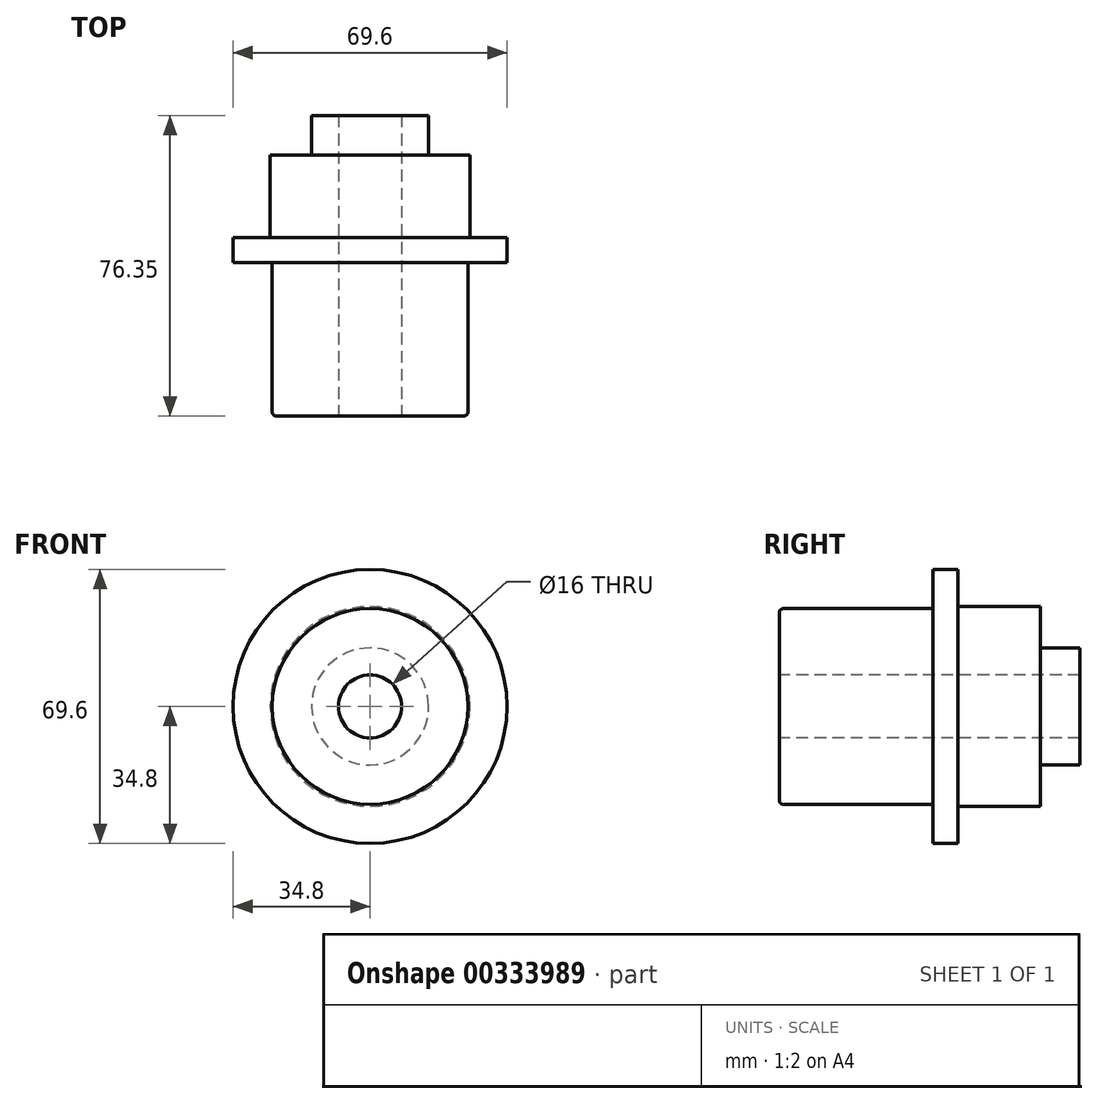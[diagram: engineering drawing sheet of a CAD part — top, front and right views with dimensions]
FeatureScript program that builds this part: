
annotation { "Feature Type Name" : "Feature", "Feature Type Description" : "" }
export const myFeature = defineFeature(function(context is Context, id is Id, definition is map)
    precondition{}
    {
        {
            var Q0;
            Q0=qCreatedBy(makeId("Front.planeOp"),FACE);
            var sketch = newSketch(context, id + "F0", { "sketchPlane" : qUnion([Q0])});
            skCircle(sketch, "E0", {"center": v(0, 0) * mm, "radius": 34.8 * mm});
            skSolve(sketch);
        }
        {
            var Q0;
            Q0 = qSketchRegion(id + "F0", true);
            extrude(context, id + "F1", {"entities" : qUnion([Q0]), "depth" : 6.35 * mm});
        }
        {
            var Q0;
            Q0=makeQuery(id+"F1.opExtrude","CAP_FACE",FACE,{"disambiguationData":[OSD([sQuery(id+"F0.wireOp",EDGE,"E0")])],"isStart":false});
            var sketch = newSketch(context, id + "F2", { "sketchPlane" : qUnion([Q0])});
            skCircle(sketch, "E1", {"center": v(0, 0) * mm, "radius": 24.85 * mm});
            skSolve(sketch);
        }
        {
            var Q0;
            Q0 = qSketchRegion(id + "F2", true);
            extrude(context, id + "F3", {"entities" : qUnion([Q0]), "operationType" : NewBodyOperationType.ADD, "depth" : 39 * mm});
        }
        {
            var Q0;
            Q0=makeQuery(id+"F3.opExtrude","CAP_EDGE",EDGE,{"disambiguationData":[OSD([sQuery(id+"F2.wireOp",EDGE,"E1")])],"isStart":false});
            fillet(context, id + "F4", {"entities" : qUnion([Q0]), "radius" : 1 * mm, "tangentPropagation" : true, "allowEdgeOverflow" : false});
        }
        {
            var Q0;
            Q0=makeQuery(id+"F1.opExtrude","CAP_FACE",FACE,{"disambiguationData":[OSD([sQuery(id+"F0.wireOp",EDGE,"E0")])],"isStart":true});
            var sketch = newSketch(context, id + "F5", { "sketchPlane" : qUnion([Q0])});
            skCircle(sketch, "E2", {"center": v(0, 0) * mm, "radius": 25.36 * mm});
            skSolve(sketch);
        }
        {
            var Q0;
            Q0 = qSketchRegion(id + "F5", true);
            extrude(context, id + "F6", {"entities" : qUnion([Q0]), "operationType" : NewBodyOperationType.ADD, "depth" : 21 * mm});
        }
        {
            var Q0;
            Q0=makeQuery(id+"F6.opExtrude","CAP_FACE",FACE,{"disambiguationData":[OSD([sQuery(id+"F5.wireOp",EDGE,"E2")])],"isStart":false});
            var sketch = newSketch(context, id + "F7", { "sketchPlane" : qUnion([Q0])});
            skCircle(sketch, "E3", {"center": v(0, 0) * mm, "radius": 14.86 * mm});
            skSolve(sketch);
        }
        {
            var Q0;
            Q0 = qSketchRegion(id + "F7", true);
            extrude(context, id + "F8", {"entities" : qUnion([Q0]), "operationType" : NewBodyOperationType.ADD, "depth" : 10 * mm});
        }
        {
            var Q0;
            Q0=makeQuery(id+"F3.opExtrude","CAP_FACE",FACE,{"disambiguationData":[OSD([sQuery(id+"F2.wireOp",EDGE,"E1")])],"isStart":false});
            var sketch = newSketch(context, id + "F9", { "sketchPlane" : qUnion([Q0])});
            skPoint(sketch, "E4", {"position": v(0, 0) * mm});
            skSolve(sketch);
        }
        {
            var Q0;
            Q0=sQuery(id+"F9.wireOp",VERTEX,"E4");
            var Q1;
            Q1=makeQuery(id+"F1.opExtrude","SWEPT_BODY",BODY,{"disambiguationData":[OSD([sQuery(id+"F0.wireOp",EDGE,"E0")])]});
            hole(context, id + "F10", {"style" : HoleStyle.SIMPLE, "endStyle" : HoleEndStyle.THROUGH, "holeDiameter" : 16 * mm, "majorDiameter" : 5 * mm, "tappedDepth" : 12 * mm, "tapClearance" : 3, "startFromSketch" : true, "locations" : qUnion([Q0]), "scope" : qUnion([Q1])});
        }
    });
